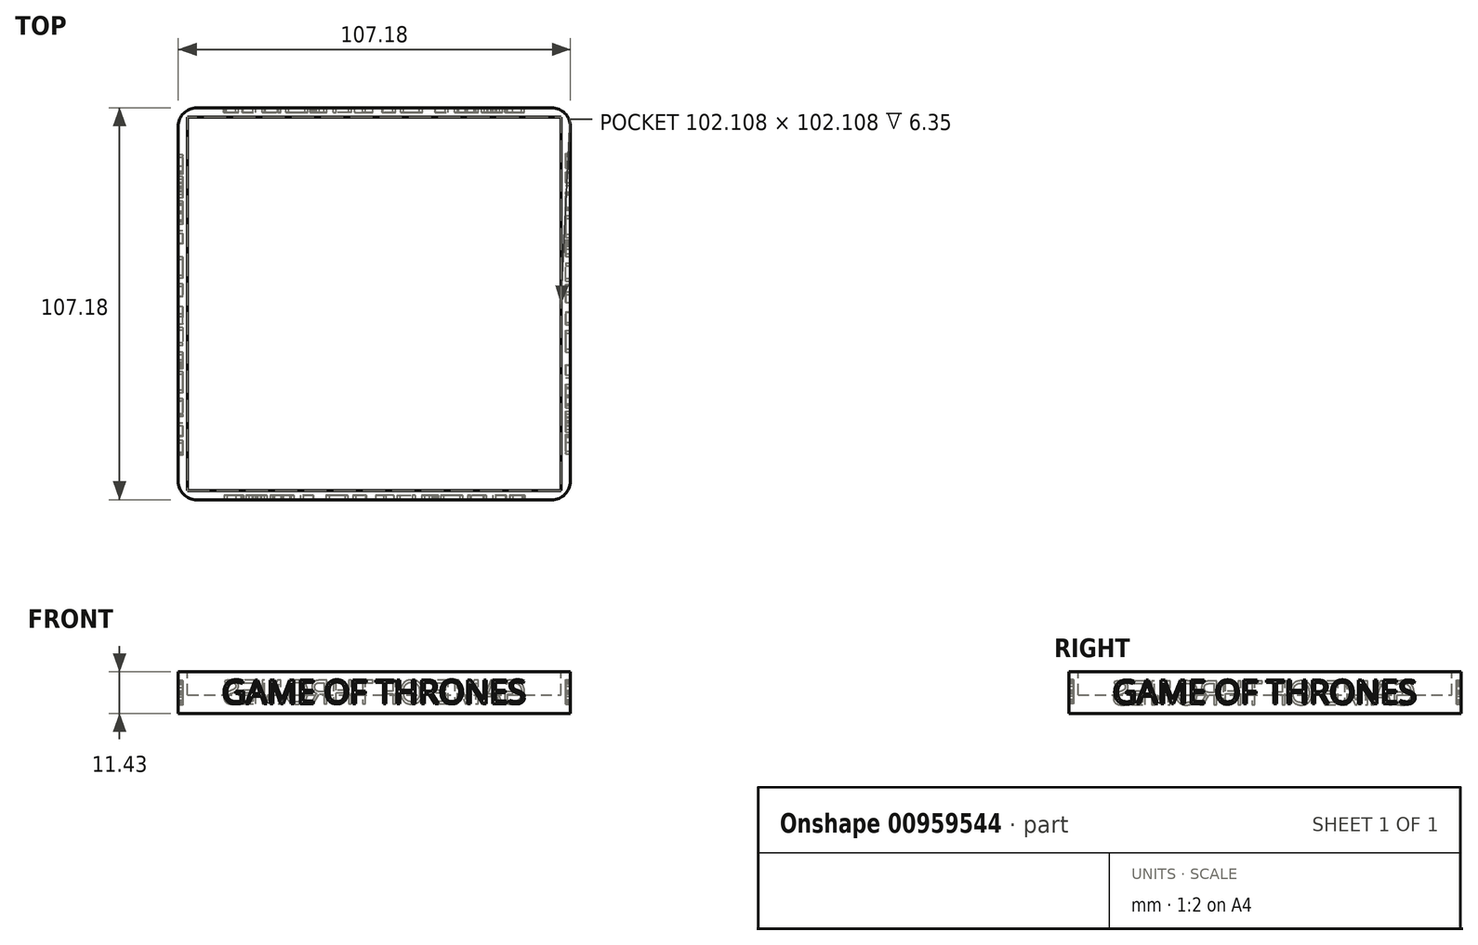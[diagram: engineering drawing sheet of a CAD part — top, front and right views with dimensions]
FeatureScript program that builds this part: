
annotation { "Feature Type Name" : "Feature", "Feature Type Description" : "" }
export const myFeature = defineFeature(function(context is Context, id is Id, definition is map)
    precondition{}
    {
        {
            var Q0;
            Q0=qCreatedBy(makeId("Top.planeOp"),FACE);
            var sketch = newSketch(context, id + "F0", { "sketchPlane" : qUnion([Q0])});
            skLineSegment(sketch, "E0.bottom", {"start": v(-53.6, -53.6) * mm, "end": v(53.6, -53.6) * mm});
            skLineSegment(sketch, "E0.top", {"start": v(-53.6, 53.6) * mm, "end": v(53.6, 53.6) * mm});
            skLineSegment(sketch, "E0.left", {"start": v(-53.6, -53.6) * mm, "end": v(-53.6, 53.6) * mm});
            skLineSegment(sketch, "E0.right", {"start": v(53.6, -53.6) * mm, "end": v(53.6, 53.6) * mm});
            skPoint(sketch, "E0.middle", {"position": v(0, 0) * mm});
            skSolve(sketch);
        }
        {
            var Q0;
            Q0 = qSketchRegion(id + "F0", true);
            extrude(context, id + "F1", {"entities" : qUnion([Q0]), "oppositeDirection" : true, "depth" : 11.43 * mm, "offsetDistance" : 25.4 * mm});
        }
        {
            var Q0;
            Q0=makeQuery(id+"F1.opExtrude","SWEPT_EDGE",EDGE,{"disambiguationData":[OSD([sQuery(id+"F0.wireOp",EDGE,"E0.top"),sQuery(id+"F0.wireOp",EDGE,"E0.left")])]});
            var Q1;
            Q1=makeQuery(id+"F1.opExtrude","SWEPT_EDGE",EDGE,{"disambiguationData":[OSD([sQuery(id+"F0.wireOp",EDGE,"E0.bottom"),sQuery(id+"F0.wireOp",EDGE,"E0.left")])]});
            var Q2;
            Q2=makeQuery(id+"F1.opExtrude","SWEPT_EDGE",EDGE,{"disambiguationData":[OSD([sQuery(id+"F0.wireOp",EDGE,"E0.top"),sQuery(id+"F0.wireOp",EDGE,"E0.right")])]});
            var Q3;
            Q3=makeQuery(id+"F1.opExtrude","SWEPT_EDGE",EDGE,{"disambiguationData":[OSD([sQuery(id+"F0.wireOp",EDGE,"E0.bottom"),sQuery(id+"F0.wireOp",EDGE,"E0.right")])]});
            fillet(context, id + "F2", {"entities" : qUnion([Q0, Q1, Q2, Q3]), "radius" : 5.08 * mm, "tangentPropagation" : true, "allowEdgeOverflow" : false});
        }
        {
            var Q0;
            Q0=makeQuery(id+"F1.opExtrude","CAP_FACE",FACE,{"disambiguationData":[OSD([sQuery(id+"F0.wireOp",EDGE,"E0.bottom"),sQuery(id+"F0.wireOp",EDGE,"E0.top"),sQuery(id+"F0.wireOp",EDGE,"E0.left"),sQuery(id+"F0.wireOp",EDGE,"E0.right")])],"isStart":true});
            var sketch = newSketch(context, id + "F3", { "sketchPlane" : qUnion([Q0])});
            skLineSegment(sketch, "E1.bottom", {"start": v(-51.05, -51.05) * mm, "end": v(51.05, -51.05) * mm});
            skLineSegment(sketch, "E1.top", {"start": v(-51.05, 51.05) * mm, "end": v(51.05, 51.05) * mm});
            skLineSegment(sketch, "E1.left", {"start": v(-51.05, -51.05) * mm, "end": v(-51.05, 51.05) * mm});
            skLineSegment(sketch, "E1.right", {"start": v(51.05, -51.05) * mm, "end": v(51.05, 51.05) * mm});
            skPoint(sketch, "E1.middle", {"position": v(0, 0) * mm});
            skSolve(sketch);
        }
        {
            var Q0;
            Q0 = qSketchRegion(id + "F3", true);
            extrude(context, id + "F4", {"entities" : qUnion([Q0]), "operationType" : NewBodyOperationType.REMOVE, "oppositeDirection" : true, "depth" : 6.35 * mm, "offsetDistance" : 25.4 * mm});
        }
        {
            var Q0;
            Q0=makeQuery(id+"F1.opExtrude","SWEPT_FACE",FACE,{"disambiguationData":[OSD([sQuery(id+"F0.wireOp",EDGE,"E0.left")])]});
            var sketch = newSketch(context, id + "F5", { "sketchPlane" : qUnion([Q0])});
            skText(sketch, "E2", { "text": "GAME OF THRONES", "fontName": "OpenSans-Regular.ttf"});
            const initialGuessF5  = {"E2": [-0.04131, -0.00903, 1, 0, 0.00652]};
            skSetInitialGuess(sketch, initialGuessF5);
            skSolve(sketch);
        }
        {
            var Q0;
            Q0 = qSketchRegion(id + "F5", true);
            extrude(context, id + "F6", {"entities" : qUnion([Q0]), "operationType" : NewBodyOperationType.REMOVE, "oppositeDirection" : true, "depth" : 1.27 * mm, "offsetDistance" : 25.4 * mm});
        }
        {
            var Q0;
            Q0=makeQuery(id+"F1.opExtrude","SWEPT_FACE",FACE,{"disambiguationData":[OSD([sQuery(id+"F0.wireOp",EDGE,"E0.top")])]});
            var sketch = newSketch(context, id + "F7", { "sketchPlane" : qUnion([Q0])});
            skText(sketch, "E3", { "text": "GAME OF THRONES", "fontName": "OpenSans-Regular.ttf"});
            const initialGuessF7  = {"E3": [-0.0416, -0.0088, 1, 0, 0.00652]};
            skSetInitialGuess(sketch, initialGuessF7);
            skSolve(sketch);
        }
        {
            var Q0;
            Q0=makeQuery(id+"F1.opExtrude","SWEPT_FACE",FACE,{"disambiguationData":[OSD([sQuery(id+"F0.wireOp",EDGE,"E0.right")])]});
            var sketch = newSketch(context, id + "F8", { "sketchPlane" : qUnion([Q0])});
            skText(sketch, "E4", { "text": "GAME OF THRONES", "fontName": "OpenSans-Regular.ttf"});
            skPoint(sketch, "E5", {"position": v(0, -11.43) * mm});
            const initialGuessF8  = {"E4": [-0.04162, -0.00879, 1, 0, 0.00652]};
            skSetInitialGuess(sketch, initialGuessF8);
            skSolve(sketch);
        }
        {
            var Q0;
            Q0=makeQuery(id+"F1.opExtrude","SWEPT_FACE",FACE,{"disambiguationData":[OSD([sQuery(id+"F0.wireOp",EDGE,"E0.bottom")])]});
            var sketch = newSketch(context, id + "F9", { "sketchPlane" : qUnion([Q0])});
            skText(sketch, "E6", { "text": "GAME OF THRONES", "fontName": "OpenSans-Regular.ttf"});
            const initialGuessF9  = {"E6": [-0.04163, -0.00874, 1, 0, 0.00652]};
            skSetInitialGuess(sketch, initialGuessF9);
            skSolve(sketch);
        }
        {
            var Q0;
            Q0 = qSketchRegion(id + "F9", true);
            extrude(context, id + "F10", {"entities" : qUnion([Q0]), "operationType" : NewBodyOperationType.REMOVE, "oppositeDirection" : true, "depth" : 1.27 * mm, "offsetDistance" : 25.4 * mm});
        }
        {
            var Q0;
            Q0 = qSketchRegion(id + "F8", true);
            extrude(context, id + "F11", {"entities" : qUnion([Q0]), "operationType" : NewBodyOperationType.REMOVE, "oppositeDirection" : true, "depth" : 1.27 * mm, "offsetDistance" : 25.4 * mm});
        }
        {
            var Q0;
            Q0 = qSketchRegion(id + "F7", true);
            extrude(context, id + "F12", {"entities" : qUnion([Q0]), "operationType" : NewBodyOperationType.REMOVE, "oppositeDirection" : true, "depth" : 1.27 * mm, "offsetDistance" : 25.4 * mm});
        }
    });
